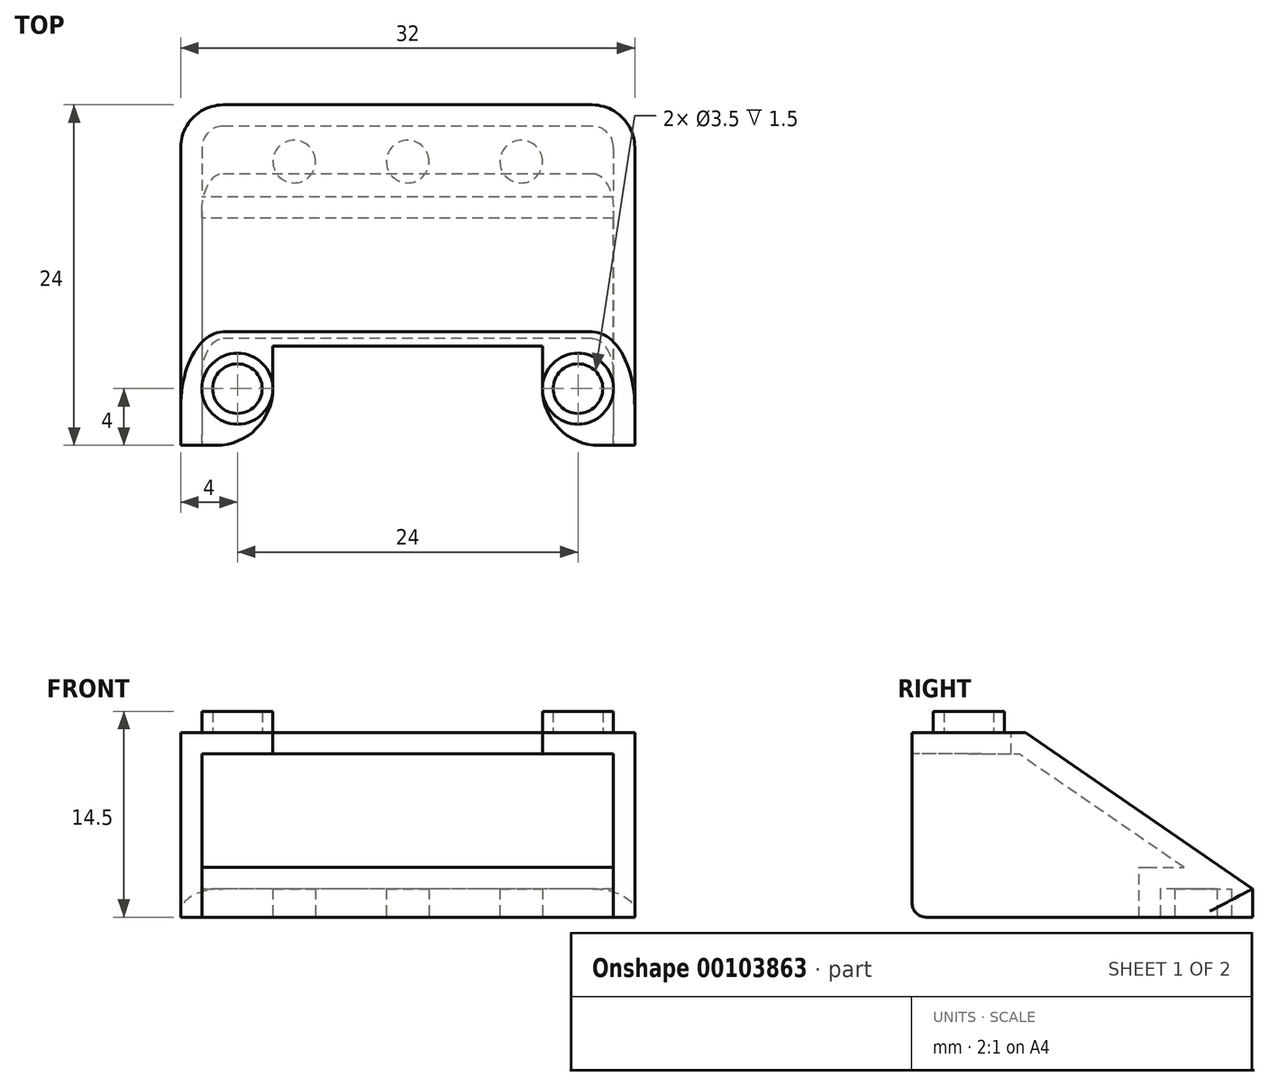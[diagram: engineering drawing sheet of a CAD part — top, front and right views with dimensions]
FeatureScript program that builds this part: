
annotation { "Feature Type Name" : "Feature", "Feature Type Description" : "" }
export const myFeature = defineFeature(function(context is Context, id is Id, definition is map)
    precondition{}
    {
        {
            var Q0;
            Q0=qCreatedBy(makeId("Right.planeOp"),FACE);
            var sketch = newSketch(context, id + "F0", { "sketchPlane" : qUnion([Q0])});
            skLineSegment(sketch, "E0.bottom", {"start": v(-4, 6.5) * mm, "end": v(-12, 6.5) * mm});
            skLineSegment(sketch, "E0.top", {"start": v(12, -6.5) * mm, "end": v(-12, -6.5) * mm});
            skLineSegment(sketch, "E0.left", {"start": v(12, -4.5) * mm, "end": v(12, -6.5) * mm});
            skLineSegment(sketch, "E0.right", {"start": v(-12, 6.5) * mm, "end": v(-12, -6.5) * mm});
            skPoint(sketch, "E0.middle", {"position": v(0, 0) * mm});
            skLineSegment(sketch, "E1", {"start": v(-4, 6.5) * mm, "end": v(12, -4.5) * mm});
            skSolve(sketch);
        }
        {
            var Q0;
            Q0 = qSketchRegion(id + "F0", true);
            extrude(context, id + "F1", {"entities" : qUnion([Q0]), "depth" : 32 * mm, "symmetric" : true});
        }
        {
            var Q0;
            Q0=makeQuery(id+"F1.opExtrude","CAP_EDGE",EDGE,{"disambiguationData":[OSD([sQuery(id+"F0.wireOp",EDGE,"E0.left")])],"isStart":false});
            var Q1;
            Q1=makeQuery(id+"F1.opExtrude","CAP_EDGE",EDGE,{"disambiguationData":[OSD([sQuery(id+"F0.wireOp",EDGE,"E0.left")])],"isStart":true});
            var Q2;
            Q2=makeQuery(id+"F1.opExtrude","CAP_EDGE",EDGE,{"disambiguationData":[OSD([sQuery(id+"F0.wireOp",EDGE,"E1")])],"isStart":false});
            var Q3;
            Q3=makeQuery(id+"F1.opExtrude","CAP_EDGE",EDGE,{"disambiguationData":[OSD([sQuery(id+"F0.wireOp",EDGE,"E1")])],"isStart":true});
            fillet(context, id + "F2", {"entities" : qUnion([Q0, Q1, Q2, Q3]), "radius" : 3 * mm, "tangentPropagation" : true, "allowEdgeOverflow" : false});
        }
        {
            var Q0;
            Q0=makeQuery(id+"F1.opExtrude","SWEPT_FACE",FACE,{"disambiguationData":[OSD([sQuery(id+"F0.wireOp",EDGE,"E0.top")])]});
            var sketch = newSketch(context, id + "F3", { "sketchPlane" : qUnion([Q0])});
            skLineSegment(sketch, "E2.0", {"start": v(14.5, -9) * mm, "end": v(14.5, -5.5) * mm});
            skLineSegment(sketch, "E2.1", {"start": v(-14.5, -9) * mm, "end": v(-14.5, -5.5) * mm});
            skArc(sketch, "E2.2", {"start": v(-14.5, -9) * mm, "mid": v(-14.06, -10.06) * mm, "end": v(-13, -10.5) * mm});
            skLineSegment(sketch, "E2.3", {"start": v(13, -10.5) * mm, "end": v(-13, -10.5) * mm});
            skArc(sketch, "E2.4", {"start": v(13, -10.5) * mm, "mid": v(14.06, -10.06) * mm, "end": v(14.5, -9) * mm});
            skLineSegment(sketch, "E3.0", {"start": v(14.5, -5.5) * mm, "end": v(-14.5, -5.5) * mm});
            skCircle(sketch, "E4", {"center": v(-8, -8) * mm, "radius": 1.5 * mm});
            skLineSegment(sketch, "E5", {"start": v(0, -5.5) * mm, "end": v(0, -10.5) * mm, "construction": true});
            skCircle(sketch, "E6.1.0.0", {"center": v(0, -8) * mm, "radius": 1.5 * mm});
            skCircle(sketch, "E6.2.0.0", {"center": v(8, -8) * mm, "radius": 1.5 * mm});
            skLineSegment(sketch, "E6.direction1", {"start": v(-8, -8) * mm, "end": v(0, -8) * mm, "construction": true});
            skSolve(sketch);
        }
        {
            var Q0;
            Q0=makeQuery(id+"F3.imprint","IMPRINT",FACE,{"disambiguationData":[TD([[makeQuery(id+"F3.imprint","IMPRINT",EDGE,{"derivedFrom":sQuery(id+"F3.wireOp",EDGE,"E2.0")}),1.0]])]});
            extrude(context, id + "F4", {"entities" : qUnion([Q0]), "operationType" : NewBodyOperationType.REMOVE, "oppositeDirection" : true, "depth" : 2 * mm});
        }
        {
            var Q0;
            Q0=makeQuery(id+"F1.opExtrude","SWEPT_FACE",FACE,{"disambiguationData":[OSD([sQuery(id+"F0.wireOp",EDGE,"E0.right")])]});
            var Q1;
            {var subQ0=sQuery(id+"F0.wireOp",EDGE,"E0.left");var subQ3=sQuery(id+"F0.wireOp",EDGE,"E0.top");Q1=makeQuery(id+"F4.boolean.opBoolean","SPLIT",FACE,{"disambiguationData":[TD([makeQuery(id+"F1.opExtrude","SWEPT_FACE",FACE,{"disambiguationData":[OSD([subQ0])]})])],"derivedFrom":makeQuery(id+"F1.opExtrude","SWEPT_FACE",FACE,{"disambiguationData":[OSD([subQ3])]})});}
            shell(context, id + "F5", {"entities" : qUnion([Q0, Q1]), "thickness" : 1.5 * mm});
        }
        {
            var Q0;
            Q0=makeQuery(id+"F1.opExtrude","SWEPT_FACE",FACE,{"disambiguationData":[OSD([sQuery(id+"F0.wireOp",EDGE,"E0.bottom")])]});
            var sketch = newSketch(context, id + "F6", { "sketchPlane" : qUnion([Q0])});
            skLineSegment(sketch, "E7", {"start": v(-9.5, -5) * mm, "end": v(9.5, -5) * mm});
            skLineSegment(sketch, "E8", {"start": v(-9.5, -5) * mm, "end": v(-9.5, -8) * mm});
            skLineSegment(sketch, "E9", {"start": v(9.5, -5) * mm, "end": v(9.5, -8) * mm});
            skArc(sketch, "E10", {"start": v(-9.5, -8) * mm, "mid": v(-10.67, -10.83) * mm, "end": v(-13.5, -12) * mm});
            skArc(sketch, "E11", {"start": v(9.5, -8) * mm, "mid": v(10.67, -10.83) * mm, "end": v(13.5, -12) * mm});
            skCircle(sketch, "E12", {"center": v(-12, -8) * mm, "radius": 2.5 * mm});
            skLineSegment(sketch, "E13", {"start": v(0, -4) * mm, "end": v(0, -12) * mm, "construction": true});
            skCircle(sketch, "E14", {"center": v(12, -8) * mm, "radius": 2.5 * mm});
            skCircle(sketch, "E15.0", {"center": v(-12, -8) * mm, "radius": 1.75 * mm});
            skCircle(sketch, "E16", {"center": v(12, -8) * mm, "radius": 1.75 * mm});
            skSolve(sketch);
        }
        {
            var Q0;
            Q0=makeQuery(id+"F6.imprint","IMPRINT",FACE,{"disambiguationData":[TD([[makeQuery(id+"F6.imprint","IMPRINT",EDGE,{"derivedFrom":sQuery(id+"F6.wireOp",EDGE,"E7")}),-1.0]])]});
            extrude(context, id + "F7", {"entities" : qUnion([Q0]), "operationType" : NewBodyOperationType.REMOVE, "endBound" : BoundingType.THROUGH_ALL, "oppositeDirection" : true, "depth" : 25 * mm});
        }
        {
            var Q0;
            Q0=makeQuery(id+"F6.imprint","IMPRINT",FACE,{"disambiguationData":[TD([[makeQuery(id+"F6.imprint","IMPRINT",EDGE,{"derivedFrom":sQuery(id+"F6.wireOp",EDGE,"E12")}),1.0]])]});
            var Q1;
            Q1=makeQuery(id+"F6.imprint","IMPRINT",FACE,{"disambiguationData":[TD([[makeQuery(id+"F6.imprint","IMPRINT",EDGE,{"derivedFrom":sQuery(id+"F6.wireOp",EDGE,"E14")}),1.0]])]});
            extrude(context, id + "F8", {"entities" : qUnion([Q0, Q1]), "operationType" : NewBodyOperationType.ADD, "depth" : 1.5 * mm});
        }
        {
            var Q0;
            Q0=makeQuery(id+"F5.opShell","OFFSET_EDGE",EDGE,{"disambiguationData":[OSD([sQuery(id+"F0.wireOp",EDGE,"E0.top"),sQuery(id+"F0.wireOp",EDGE,"E0.right")])]});
            var Q1;
            Q1=makeQuery(id+"F1.opExtrude","SWEPT_EDGE",EDGE,{"disambiguationData":[OSD([sQuery(id+"F0.wireOp",EDGE,"E0.top"),sQuery(id+"F0.wireOp",EDGE,"E0.right")])]});
            fillet(context, id + "F9", {"entities" : qUnion([Q0, Q1]), "radius" : 1 * mm, "tangentPropagation" : true, "allowEdgeOverflow" : false});
        }
    });
